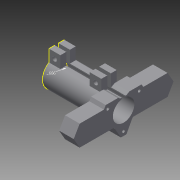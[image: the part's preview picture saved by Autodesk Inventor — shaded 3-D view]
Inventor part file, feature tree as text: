
AUTODESK INVENTOR PART (.ipt)
format: ipt  version: 2013 SP2 (Build 170200200, 200)  size: 228,864 bytes
history: native  units: in
note: dims shown in document units (in); Inventor stores cm internally (conversion verified against a paired STEP export)
features: extrude x5, sketch x5, thicken_offset x2, mirror x1
ambient origin geometry x8: Origin, YZ Plane, XZ Plane, XY Plane, X Axis, Y Axis, Z Axis, Center Point
bodies: Solid1 (feature_tree)
feature tree (13):
  extrude  "Extrusion1"  Depth=0.2in
  extrude  "Extrusion2"  Depth=0.4in
  extrude  "Extrusion3"  Depth=0.456in TaperAngle=0.0deg
  mirror  "Mirror1"
  thicken_offset  "Thicken1"
  thicken_offset  "Thicken2"
  extrude  "Extrusion4"  Depth=0.5in TaperAngle=0.0deg
  sketch  "Sketch8"  dims[d11=0.71in d13=0.5in d14=0.0in]
  extrude  "Extrusion5"  Depth=0.2in
  sketch  "Sketch1"  dims[d0=0.4in d1=0.2in]
  sketch  "Sketch2"  dims[d3=0.125in d4=0.4in]
  sketch  "Sketch3"  dims[d5=0.2in d6=0.456in d7=0.0in]
  sketch  "Sketch9"  dims[d15=0.9in d16=0.0in d17=0.2in d19=0.2in d20=0.155in d21=1.0in d22=0.0in d45=0.5in d46=0.5in d47=0.5in d48=0.5in d51=0.5in d52=0.0in d53=0.666in d54=0.735in d55=10.0in d56=0.0in]
